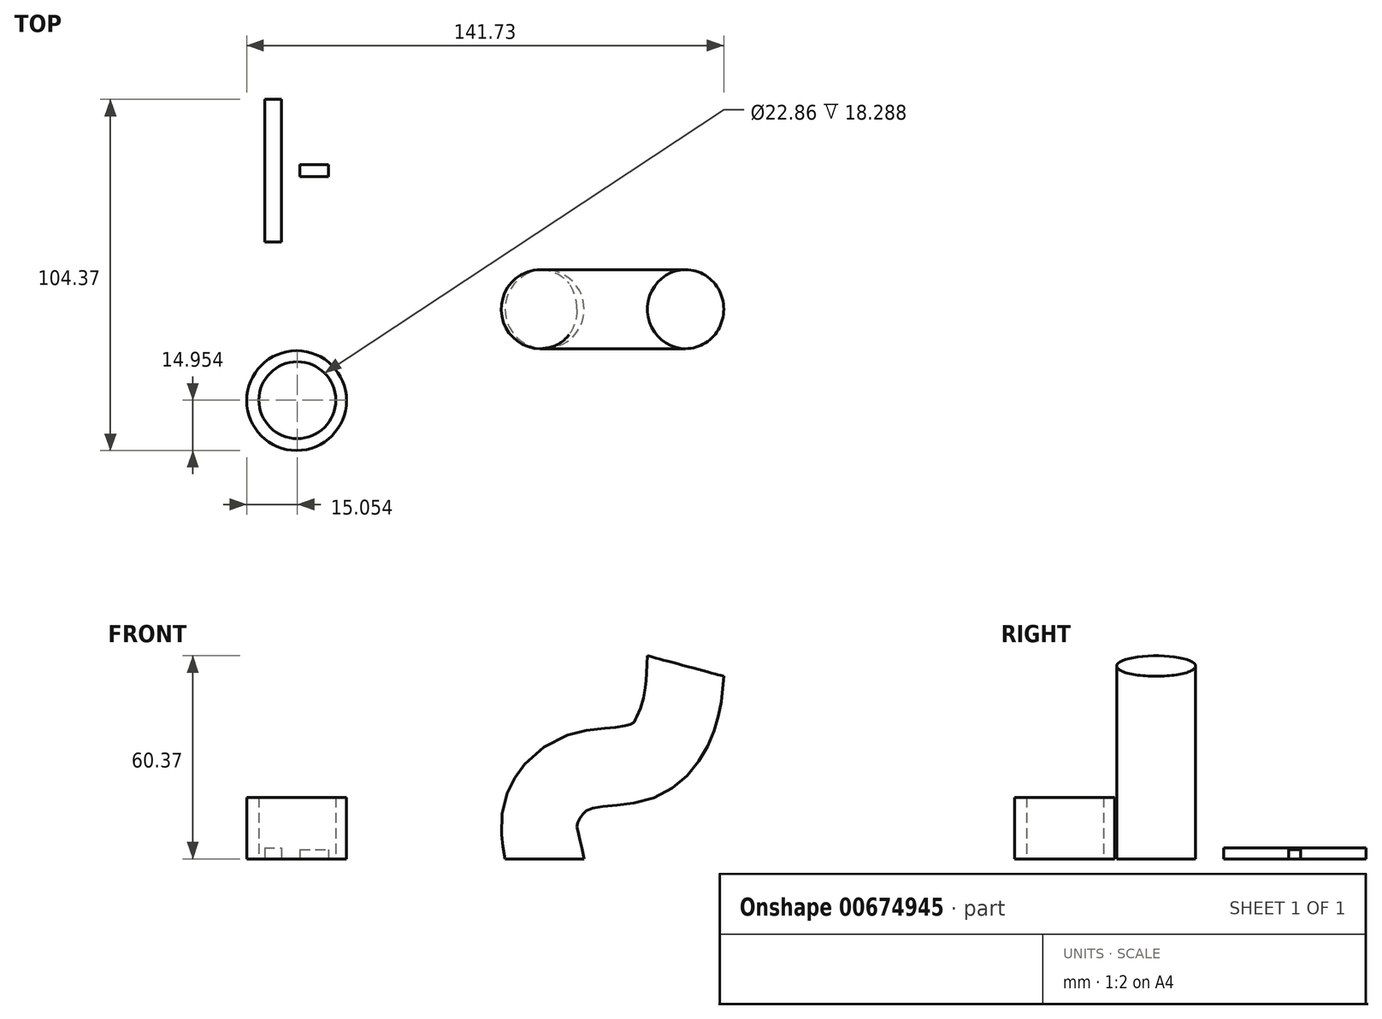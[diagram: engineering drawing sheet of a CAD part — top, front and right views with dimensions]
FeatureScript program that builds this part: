
annotation { "Feature Type Name" : "Feature", "Feature Type Description" : "" }
export const myFeature = defineFeature(function(context is Context, id is Id, definition is map)
    precondition{}
    {
        {
            var Q0;
            Q0=qCreatedBy(makeId("Top.planeOp"),FACE);
            var sketch = newSketch(context, id + "F0", { "sketchPlane" : qUnion([Q0])});
            skLineSegment(sketch, "E0.bottom", {"start": v(-53.6, 62.37) * mm, "end": v(-48.58, 62.37) * mm});
            skLineSegment(sketch, "E0.top", {"start": v(-53.6, 20.01) * mm, "end": v(-48.58, 20.01) * mm});
            skLineSegment(sketch, "E0.left", {"start": v(-53.6, 62.37) * mm, "end": v(-53.6, 20.01) * mm});
            skLineSegment(sketch, "E0.right", {"start": v(-48.58, 62.37) * mm, "end": v(-48.58, 20.01) * mm});
            skLineSegment(sketch, "E1.bottom", {"start": v(-43.65, 43.42) * mm, "end": v(-34.41, 43.42) * mm});
            skLineSegment(sketch, "E1.top", {"start": v(-43.65, 40.48) * mm, "end": v(-34.41, 40.48) * mm});
            skLineSegment(sketch, "E1.left", {"start": v(-43.65, 43.42) * mm, "end": v(-43.65, 40.48) * mm});
            skLineSegment(sketch, "E1.right", {"start": v(-34.41, 43.42) * mm, "end": v(-34.41, 40.48) * mm});
            skSolve(sketch);
        }
        {
            var Q0;
            Q0=makeQuery(id+"F0.imprint","IMPRINT",FACE,{"disambiguationData":[TD([[makeQuery(id+"F0.imprint","IMPRINT",EDGE,{"derivedFrom":sQuery(id+"F0.wireOp",EDGE,"E0.bottom")}),-1.0]])]});
            extrude(context, id + "F1", {"entities" : qUnion([Q0]), "depth" : 3.3 * mm, "offsetDistance" : 25.4 * mm});
        }
        {
            var Q0;
            Q0=qCreatedBy(makeId("Top.planeOp"),FACE);
            var sketch = newSketch(context, id + "F2", { "sketchPlane" : qUnion([Q0])});
            skLineSegment(sketch, "E2.bottom", {"start": v(-43.16, 42.9) * mm, "end": v(-34.64, 42.9) * mm});
            skLineSegment(sketch, "E2.top", {"start": v(-43.16, 39.4) * mm, "end": v(-34.64, 39.4) * mm});
            skLineSegment(sketch, "E2.left", {"start": v(-43.16, 42.9) * mm, "end": v(-43.16, 39.4) * mm});
            skLineSegment(sketch, "E2.right", {"start": v(-34.64, 42.9) * mm, "end": v(-34.64, 39.4) * mm});
            skSolve(sketch);
        }
        {
            var Q0;
            Q0=makeQuery(id+"F2.imprint","IMPRINT",FACE,{"disambiguationData":[TD([[makeQuery(id+"F2.imprint","IMPRINT",EDGE,{"derivedFrom":sQuery(id+"F2.wireOp",EDGE,"E2.bottom")}),-1.0]])]});
            extrude(context, id + "F3", {"entities" : qUnion([Q0]), "depth" : 2.8 * mm, "offsetDistance" : 25.4 * mm});
        }
        {
            var Q0;
            Q0=qCreatedBy(makeId("Top.planeOp"),FACE);
            var sketch = newSketch(context, id + "F4", { "sketchPlane" : qUnion([Q0])});
            skCircle(sketch, "E3", {"center": v(-44.11, -27.17) * mm, "radius": 14.83 * mm});
            skSolve(sketch);
        }
        {
            var Q0;
            Q0=makeQuery(id+"F4.imprint","IMPRINT",FACE,{"disambiguationData":[TD([[makeQuery(id+"F4.imprint","IMPRINT",EDGE,{"derivedFrom":sQuery(id+"F4.wireOp",EDGE,"E3")}),1.0]])]});
            extrude(context, id + "F5", {"entities" : qUnion([Q0]), "depth" : 18.29 * mm, "offsetDistance" : 25.4 * mm});
        }
        {
            var Q0;
            Q0=qCreatedBy(makeId("Top.planeOp"),FACE);
            var sketch = newSketch(context, id + "F6", { "sketchPlane" : qUnion([Q0])});
            skPoint(sketch, "E4", {"position": v(-43.89, -27.05) * mm});
            skSolve(sketch);
        }
        {
            var Q0;
            Q0=sQuery(id+"F6.wireOp",VERTEX,"E4");
            var Q1;
            Q1=makeQuery(id+"F5.opExtrude","SWEPT_BODY",BODY,{"disambiguationData":[OSD([sQuery(id+"F4.wireOp",EDGE,"E3")])]});
            hole(context, id + "F7", {"style" : HoleStyle.SIMPLE, "endStyle" : HoleEndStyle.THROUGH, "oppositeDirection" : true, "holeDiameter" : 22.86 * mm, "majorDiameter" : 6.35 * mm, "isTappedThrough" : true, "tappedDepth" : 12.7 * mm, "tapClearance" : 3, "locations" : qUnion([Q0]), "scope" : qUnion([Q1])});
        }
        {
            var Q0;
            Q0=qCreatedBy(makeId("Top.planeOp"),FACE);
            var sketch = newSketch(context, id + "F8", { "sketchPlane" : qUnion([Q0])});
            skCircle(sketch, "E5", {"center": v(29.56, 0) * mm, "radius": 11.73 * mm});
            skSolve(sketch);
        }
        {
            var Q0;
            Q0=qCreatedBy(makeId("Front.planeOp"),FACE);
            var sketch = newSketch(context, id + "F9", { "sketchPlane" : qUnion([Q0])});
            skFitSpline(sketch, "E6", {"points": [v(29.62, 0) * mm, v(29.06, 14.53) * mm, v(40.15, 25.72) * mm, v(58.7, 29.25) * mm, v(69, 41.6) * mm, v(71.52, 57.3) * mm], "startDerivative": vector(-16.06, 78.44) * mm, "endDerivative": vector(4.92, 80.02) * mm});
            skSolve(sketch);
        }
        {
            var Q0;
            Q0=makeQuery(id+"F8.imprint","IMPRINT",FACE,{"disambiguationData":[TD([[makeQuery(id+"F8.imprint","IMPRINT",EDGE,{"derivedFrom":sQuery(id+"F8.wireOp",EDGE,"E5")}),1.0]])]});
            var Q1;
            Q1=sQuery(id+"F9.wireOp",EDGE,"E6");
            sweep(context, id + "F10", {"profiles" : qUnion([Q0]), "path" : qUnion([Q1])});
        }
    });
